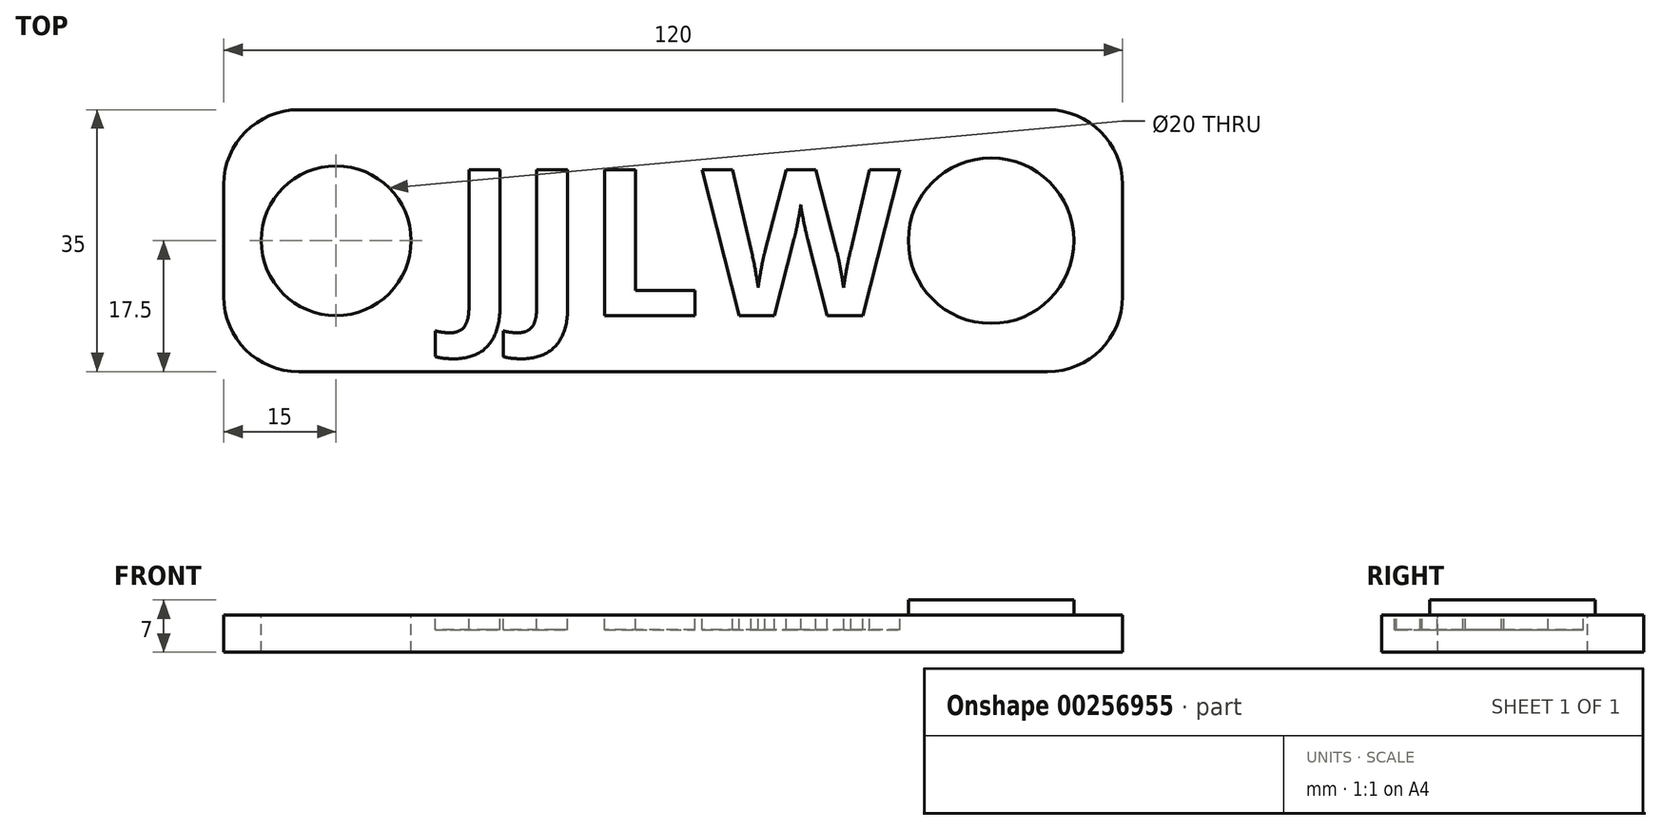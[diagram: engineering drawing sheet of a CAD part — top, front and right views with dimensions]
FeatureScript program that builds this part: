
annotation { "Feature Type Name" : "Feature", "Feature Type Description" : "" }
export const myFeature = defineFeature(function(context is Context, id is Id, definition is map)
    precondition{}
    {
        {
            var Q0;
            Q0=qCreatedBy(makeId("Top.planeOp"),FACE);
            var sketch = newSketch(context, id + "F0", { "sketchPlane" : qUnion([Q0])});
            skLineSegment(sketch, "E0.bottom", {"start": v(60, -17.5) * mm, "end": v(-60, -17.5) * mm});
            skLineSegment(sketch, "E0.top", {"start": v(60, 17.5) * mm, "end": v(-60, 17.5) * mm});
            skLineSegment(sketch, "E0.left", {"start": v(60, -17.5) * mm, "end": v(60, 17.5) * mm});
            skLineSegment(sketch, "E0.right", {"start": v(-60, -17.5) * mm, "end": v(-60, 17.5) * mm});
            skPoint(sketch, "E0.middle", {"position": v(0, 0) * mm});
            skSolve(sketch);
        }
        {
            var Q0;
            Q0=makeQuery(id+"F0.imprint","IMPRINT",FACE,{"disambiguationData":[TD([[makeQuery(id+"F0.imprint","IMPRINT",EDGE,{"derivedFrom":sQuery(id+"F0.wireOp",EDGE,"E0.bottom")}),-1.0]])]});
            extrude(context, id + "F1", {"entities" : qUnion([Q0]), "depth" : 5 * mm});
        }
        {
            var Q0;
            Q0=makeQuery(id+"F1.opExtrude","SWEPT_EDGE",EDGE,{"disambiguationData":[OSD([sQuery(id+"F0.wireOp",EDGE,"E0.bottom"),sQuery(id+"F0.wireOp",EDGE,"E0.right")])]});
            var Q1;
            Q1=makeQuery(id+"F1.opExtrude","SWEPT_EDGE",EDGE,{"disambiguationData":[OSD([sQuery(id+"F0.wireOp",EDGE,"E0.top"),sQuery(id+"F0.wireOp",EDGE,"E0.right")])]});
            var Q2;
            Q2=makeQuery(id+"F1.opExtrude","SWEPT_EDGE",EDGE,{"disambiguationData":[OSD([sQuery(id+"F0.wireOp",EDGE,"E0.top"),sQuery(id+"F0.wireOp",EDGE,"E0.left")])]});
            var Q3;
            Q3=makeQuery(id+"F1.opExtrude","SWEPT_EDGE",EDGE,{"disambiguationData":[OSD([sQuery(id+"F0.wireOp",EDGE,"E0.bottom"),sQuery(id+"F0.wireOp",EDGE,"E0.left")])]});
            fillet(context, id + "F2", {"entities" : qUnion([Q0, Q1, Q2, Q3]), "radius" : 10 * mm, "tangentPropagation" : true, "allowEdgeOverflow" : false});
        }
        {
            var Q0;
            Q0=makeQuery(id+"F1.opExtrude","CAP_FACE",FACE,{"disambiguationData":[OSD([sQuery(id+"F0.wireOp",EDGE,"E0.bottom"),sQuery(id+"F0.wireOp",EDGE,"E0.top"),sQuery(id+"F0.wireOp",EDGE,"E0.left"),sQuery(id+"F0.wireOp",EDGE,"E0.right")])],"isStart":false});
            var sketch = newSketch(context, id + "F3", { "sketchPlane" : qUnion([Q0])});
            skCircle(sketch, "E1", {"center": v(-45, 0) * mm, "radius": 10 * mm});
            skSolve(sketch);
        }
        {
            var Q0;
            Q0=makeQuery(id+"F3.imprint","IMPRINT",FACE,{"disambiguationData":[TD([[makeQuery(id+"F3.imprint","IMPRINT",EDGE,{"derivedFrom":sQuery(id+"F3.wireOp",EDGE,"E1")}),1.0]])]});
            extrude(context, id + "F4", {"entities" : qUnion([Q0]), "operationType" : NewBodyOperationType.REMOVE, "oppositeDirection" : true, "depth" : 5 * mm});
        }
        {
            var Q0;
            Q0=makeQuery(id+"F1.opExtrude","CAP_FACE",FACE,{"disambiguationData":[OSD([sQuery(id+"F0.wireOp",EDGE,"E0.bottom"),sQuery(id+"F0.wireOp",EDGE,"E0.top"),sQuery(id+"F0.wireOp",EDGE,"E0.left"),sQuery(id+"F0.wireOp",EDGE,"E0.right")])],"isStart":false});
            var sketch = newSketch(context, id + "F5", { "sketchPlane" : qUnion([Q0])});
            skText(sketch, "E2", { "text": "JJLW", "fontName": "OpenSans-Bold.ttf"});
            const initialGuessF5  = {"E2": [-0.02972, -0.01004, 1, 0, 0.01969]};
            skSetInitialGuess(sketch, initialGuessF5);
            skSolve(sketch);
        }
        {
            var Q0;
            Q0 = qSketchRegion(id + "F5", true);
            extrude(context, id + "F6", {"entities" : qUnion([Q0]), "operationType" : NewBodyOperationType.REMOVE, "oppositeDirection" : true, "depth" : 2 * mm});
        }
        {
            var Q0;
            Q0=makeQuery(id+"F1.opExtrude","CAP_FACE",FACE,{"disambiguationData":[OSD([sQuery(id+"F0.wireOp",EDGE,"E0.bottom"),sQuery(id+"F0.wireOp",EDGE,"E0.top"),sQuery(id+"F0.wireOp",EDGE,"E0.left"),sQuery(id+"F0.wireOp",EDGE,"E0.right")])],"isStart":false});
            var sketch = newSketch(context, id + "F7", { "sketchPlane" : qUnion([Q0])});
            skCircle(sketch, "E3", {"center": v(42.46, 0) * mm, "radius": 11.05 * mm});
            skSolve(sketch);
        }
        {
            var Q0;
            Q0=makeQuery(id+"F7.imprint","IMPRINT",FACE,{"disambiguationData":[TD([[makeQuery(id+"F7.imprint","IMPRINT",EDGE,{"derivedFrom":sQuery(id+"F7.wireOp",EDGE,"E3")}),1.0]])]});
            extrude(context, id + "F8", {"entities" : qUnion([Q0]), "operationType" : NewBodyOperationType.ADD, "depth" : 2 * mm});
        }
    });
